# Revit family: Портал
name_source: partatom
category: Осветительные приборы
units: mm (PartAtom-declared; Revit-internal decimal feet)

## family parameters
Всегда вертикально = Да
Источник света = Да
На основе рабочей плоскости = Нет
Общий = Нет
При загрузке вырезать с полостями = Нет
Размер круглого соединителя = Использовать диаметр
Тип детали = Нормальный
Точка расчета площади = Нет

## types (1)
- Портал
    ADSK_URL страницы изделия = https://www.allfresco.ru
    ADSK_Артикул = ДТУ371
    ADSK_Единица измерения = шт.
    ADSK_Завод-изготовитель = ALFRESCO
    ADSK_Количество фаз = 2
    ADSK_Количество фаз числовое = 0
    ADSK_Коэффициент мощности = 0
    ADSK_Масса = 57
    ADSK_Масса_Текст = 57
    ADSK_Модель = Портал ДТУ-37-AF
    ADSK_Наименование = ДТУ371 Светодиодный светильник Портал ДТУ-37-AF-85Вт
    ADSK_Напряжение = 220 В
    ADSK_Номинальная мощность = 85 Вт
    ADSK_Полная мощность = 0 В·А
    ADSK_Размер_Высота = 3600 мм
    ADSK_Ток = 0 А
    ADSK_Фактическая мощность = 80 Вт
    ADSK_Энергоэффективность = 110 лм/Вт
    H_высота треугольник профиль = 65 мм
    H_общая = 3600 мм
    H_профиль столб = 100 мм
    H_профиль столб_меньше половины = 40 мм
    H_профиль столб_половина = 50 мм
    IP Class = IP 67
    L_вылет светильник = 2200 мм
    L_длина фланца = 250 мм
    L_между отверстиями = 200 мм
    L_основание треугольник профиль = 65 мм
    L_отверстия = 30 мм
    S_ветодиодная полоса = 20 мм
    S_между отверстиями = 200 мм
    S_отверстия = 18 мм
    S_отсутп фланца = 25 мм
    S_профиль столб = 150 мм
    S_уголок = 10 мм
    S_ширина рассеиватель = 70 мм
    S_ширина фланца = 250 мм
    X_отступ до рассеивателя = 45 мм
    d_отверстий во фланце = 20 мм
    h_оси светильника = 3550 мм
    h_рассеиватель = 1 мм
    h_фланца = 10 мм
    Блок аварийного питания = Нет
    Излучение по ширине линии = 2009 мм
    Класс защиты = 1
    Класс пожароопасности = F (светильники предназначены для установки непосредственно на поверхность из нормально воспламеняемых материалов)
    Климатическая зона = УХЛ1
    Корпус светильника = Антрацит
    Область использования = Парки, скверы, общественные пространства, городская инфраструктура
    Полная установленная мощность = 0 В·А
    Рассеиватель = Белый_светодиод
    Светофильтр = 16777215
    Смещение цветовой температуры при затухании лампы = <Нет>
    Таблица выбора = Таблица параметров светильников
    Температура эксплуатации = -40 +50
    Тип ИС = LED-модуль
    Тип КСС = тип Д (косинусная)
    Тип ПРА = -
    Тип продукции = LED-светильник
    Угол наклона = 90.00°
    Файл фотометрической сетки = Portal LED 30W.ies
    Цветоывая температура = 2700-5500
